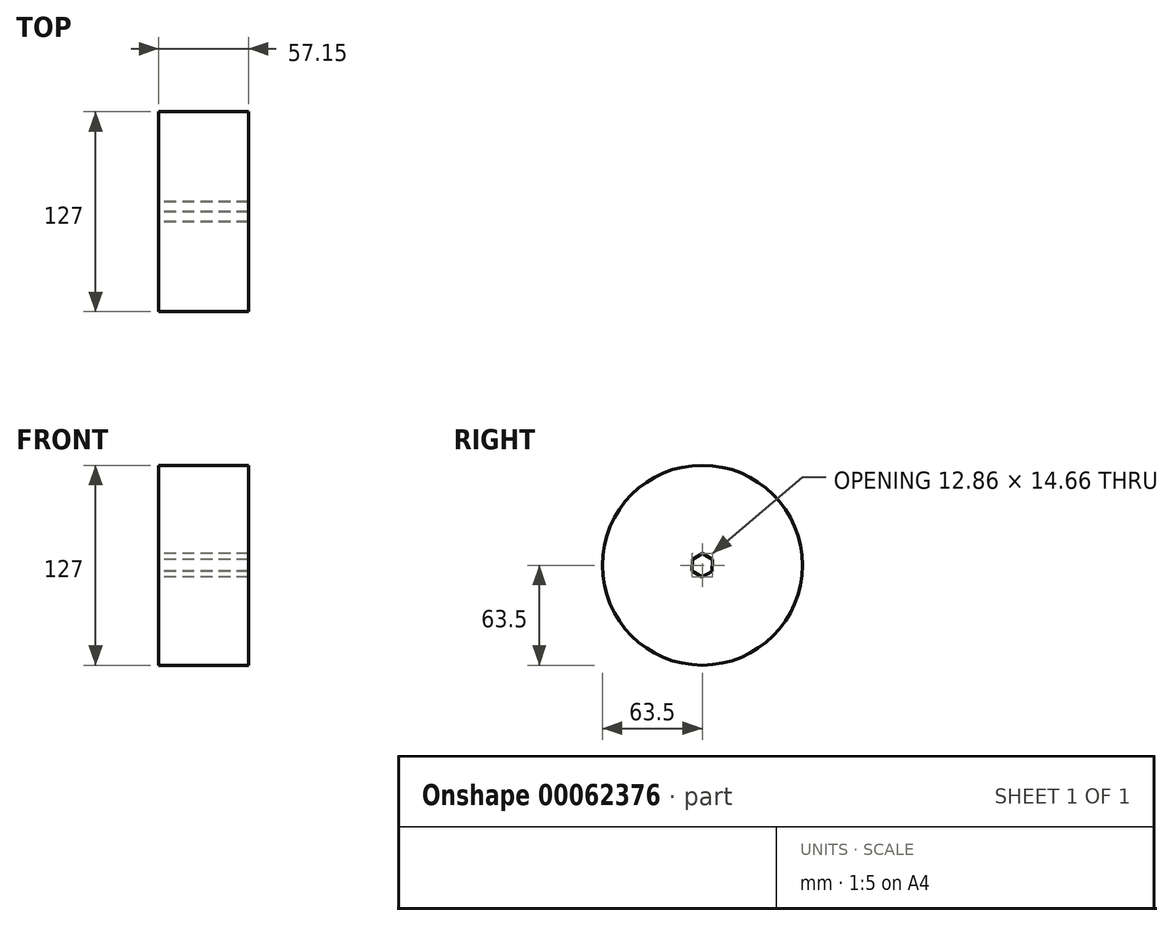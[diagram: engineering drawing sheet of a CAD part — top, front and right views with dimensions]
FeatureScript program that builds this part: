
annotation { "Feature Type Name" : "Feature", "Feature Type Description" : "" }
export const myFeature = defineFeature(function(context is Context, id is Id, definition is map)
    precondition{}
    {
        {
            var Q0;
            Q0=qCreatedBy(makeId("Right.planeOp"),FACE);
            var sketch = newSketch(context, id + "F0", { "sketchPlane" : qUnion([Q0])});
            skCircle(sketch, "E0", {"center": v(0, 0) * mm, "radius": 63.5 * mm});
            skCircle(sketch, "E1.cCircle", {"center": v(0, 0) * mm, "radius": 6.35 * mm, "construction": true});
            skLineSegment(sketch, "E1.0", {"start": v(0.17, 7.33) * mm, "end": v(6.43, 3.52) * mm});
            skLineSegment(sketch, "E1.1", {"start": v(6.43, 3.52) * mm, "end": v(6.26, -3.81) * mm});
            skLineSegment(sketch, "E1.2", {"start": v(6.26, -3.81) * mm, "end": v(-0.17, -7.33) * mm});
            skLineSegment(sketch, "E1.3", {"start": v(-0.17, -7.33) * mm, "end": v(-6.43, -3.52) * mm});
            skLineSegment(sketch, "E1.4", {"start": v(-6.43, -3.52) * mm, "end": v(-6.26, 3.81) * mm});
            skLineSegment(sketch, "E1.5", {"start": v(-6.26, 3.81) * mm, "end": v(0.17, 7.33) * mm});
            skPoint(sketch, "E1.0.midPoint", {"position": v(3.3, 5.43) * mm});
            skSolve(sketch);
        }
        {
            var Q0;
            Q0=makeQuery(id+"F0.imprint","IMPRINT",FACE,{"disambiguationData":[TD([[makeQuery(id+"F0.imprint","IMPRINT",EDGE,{"derivedFrom":sQuery(id+"F0.wireOp",EDGE,"E0")}),1.0]])]});
            extrude(context, id + "F1", {"entities" : qUnion([Q0]), "depth" : 57.15 * mm});
        }
    });
